# Revit family: Baies Linkeo avec porte avant simple largeur 800
name_source: partatom
category: Equipement spécialisé
units: mm (PartAtom-declared; Revit-internal decimal feet)

## family parameters
Basée sur le plan de construction = Non
Cote de connecteur circulaire = Utiliser le diamètre
Couper avec des vides une fois chargée = Non
Numéro OmniClass = 23.85.05.17.11.14
Partagée = Oui
Point de calcul de pièce = Non
Titre OmniClass = Multimedia Broadcasting Equipment
Toujours verticalement = Oui
Type d'élément = Normal

## types (7) — shared parameters
Avec mise à la terre = Oui
Avec porte frontale = Oui
Avec tôle de toit = Oui
Capacité de charge max = 400
Classe d'application = EC002499
Couleur = gris
Dimension modulaire = 19 pouces
Emplacement de rack = 93 mm  [stored 0.305118 ft]
Finition de surface = Poudré
Finition du rail profilé = Recourbée
Fonction = Baie Linkeo2
Indice de protection IK = IK08
Indice de protection IP = IP20
Largeur (mm) = 810 mm
Lien e-catalogue = https://www.legrand.fr
Matériau = Acier
Matériau de la porte avant = Verre
Modèle = Corps fixe
Modèle de largeur = 800 mm  [stored 2.62467 ft]
Nombre de portes = 1
RAL = 7016
Température de fonctionnement = -25°C à 70°C
Température de stockage = -25°C à 70°C
Type d'aération = Aucune
Type de montage = Frontal
Verrouillage de la porte avant = A un point
zero-valued in all types: Elévation par défaut

## per-type parameters (varying)
| type | Distance ouverture 1 | Distance ouverture 2 | EAN | Hauteur | Nombre d'unités en hauteur | Passage utile en hauteur (mm) | Passage utile en largeur (mm) | Profondeur | Profondeur du modèle | Référence Legrand | Type de montants horizontaux | Type de montants verticaux | Type de pieds de nivellement |
| Baie Linkeo2 24U 800x800 | 257 mm  [stored 0.843176 ft] | 198 mm  [stored 0.649606 ft] | 3414971001510 | 1226 mm  [stored 4.02231 ft] | 24 | 1081 mm  [stored 3.54659 ft] | 690 mm  [stored 2.26378 ft] | 830 mm  [stored 2.7231 ft] | 800 mm  [stored 2.62467 ft] | 646751 | Montants horizontaux pour armoires Linkeo  24U profondeur 800 | Montants verticaux pour armoires Linkeo  24U | Pieds de nivellement  800X800 |
| Baie Linkeo2 33U 800x800 | 257 mm  [stored 0.843176 ft] | 198 mm  [stored 0.649606 ft] | 3414971001534 | 1626 mm | 33 | 1386 mm  [stored 4.54724 ft] | 690 mm  [stored 2.26378 ft] | 830 mm  [stored 2.7231 ft] | 800 mm  [stored 2.62467 ft] | 646756 | Montants horizontaux pour armoires Linkeo  33U profondeur 800 | Montants verticaux pour armoires Linkeo  33U | Pieds de nivellement  800X800 |
| Baie Linkeo2 42U 800x600 | 57 mm  [stored 0.187008 ft] | 98 mm  [stored 0.321522 ft] | 3414971001572 | 2026 mm | 42 | 1786 mm  [stored 5.85958 ft] | 490 mm  [stored 1.60761 ft] | 630 mm  [stored 2.06693 ft] | 600 mm | 646763 | Montants horizontaux pour armoires Linkeo  42U profondeur 600 | Montants verticaux pour armoires Linkeo  42U | Pieds de nivellement  800X600 |
| Baie Linkeo2 42U 800x800 | 257 mm  [stored 0.843176 ft] | 198 mm  [stored 0.649606 ft] | 3414971001589 | 2026 mm | 42 | 1786 mm  [stored 5.85958 ft] | 690 mm  [stored 2.26378 ft] | 830 mm  [stored 2.7231 ft] | 800 mm  [stored 2.62467 ft] | 646764 | Montants horizontaux pour armoires Linkeo  42U profondeur 800 | Montants verticaux pour armoires Linkeo  42U | Pieds de nivellement  800X800 |
| Baie Linkeo2 42U 800x1000 | 457 mm  [stored 1.49934 ft] | 298 mm  [stored 0.97769 ft] | 3414971001596 | 2026 mm | 42 | 1881 mm  [stored 6.17126 ft] | 890 mm  [stored 2.91995 ft] | 1030 mm  [stored 3.37927 ft] | 1000 mm  [stored 3.28084 ft] | 646765 | Montants horizontaux pour armoires Linkeo  42U profondeur 1000 | Montants verticaux pour armoires Linkeo  42U | Pieds de nivellement  800X1000 |
| Baie Linkeo2 47U 800x800 | 257 mm  [stored 0.843176 ft] | 198 mm  [stored 0.649606 ft] | 3414971001640 | 2248 mm  [stored 7.37533 ft] | 47 | 2008 mm  [stored 6.58793 ft] | 690 mm  [stored 2.26378 ft] | 830 mm  [stored 2.7231 ft] | 800 mm  [stored 2.62467 ft] | 646773 | Montants horizontaux pour armoires Linkeo  47U profondeur 800 | Montants verticaux pour armoires Linkeo  47U | Pieds de nivellement  800X800 |
| Baie Linkeo2 47U 800x1000 | 457 mm  [stored 1.49934 ft] | 298 mm  [stored 0.97769 ft] | 3414971001657 | 2248 mm  [stored 7.37533 ft] | 47 | 2008 mm  [stored 6.58793 ft] | 890 mm  [stored 2.91995 ft] | 1030 mm  [stored 3.37927 ft] | 1000 mm  [stored 3.28084 ft] | 646774 | Montants horizontaux pour armoires Linkeo  47U profondeur 1000 | Montants verticaux pour armoires Linkeo  47U | Pieds de nivellement  800X1000 |

note: column(s) folded — value = type name in every type: Libellé BIM

note: [stored X ft] marks values corroborated as IEEE doubles in the binary element streams (Revit-internal decimal feet)
